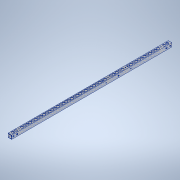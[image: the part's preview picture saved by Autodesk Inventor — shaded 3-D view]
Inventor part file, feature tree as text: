
AUTODESK INVENTOR PART (.ipt)
format: ipt  version: 2020.3 (Build 243373000, 373)  size: 307,200 bytes
history: native  units: mm
features: hole x8, sketch x8, other x1, extrude x1
ambient origin geometry x8: Origin, YZ Plane, XZ Plane, XY Plane, X Axis, Y Axis, Z Axis, Center Point
bodies: Body1 (feature_tree)
feature tree (18):
  other  "ソリッド1"
  extrude  "押し出し1"  Depth=15.0mm
  hole  "穴1"  [1 undecoded]
  hole  "穴2"  [1 undecoded]
  hole  "穴3"  [1 undecoded]
  hole  "穴4"  [1 undecoded]
  hole  "穴5"  [1 undecoded]
  hole  "穴6"  [1 undecoded]
  hole  "穴7"  [1 undecoded]
  hole  "穴8"  [1 undecoded]
  sketch  "スケッチ1"
  sketch  "スケッチ2"
  sketch  "スケッチ3"
  sketch  "スケッチ4"
  sketch  "スケッチ6"
  sketch  "スケッチ7"
  sketch  "スケッチ8"
  sketch  "スケッチ10"
note: 8 required parameter values undecoded (feature->parameter linkage not recoverable at this tier; creation-order binding heuristic only, values carry confidence <= 0.55)
